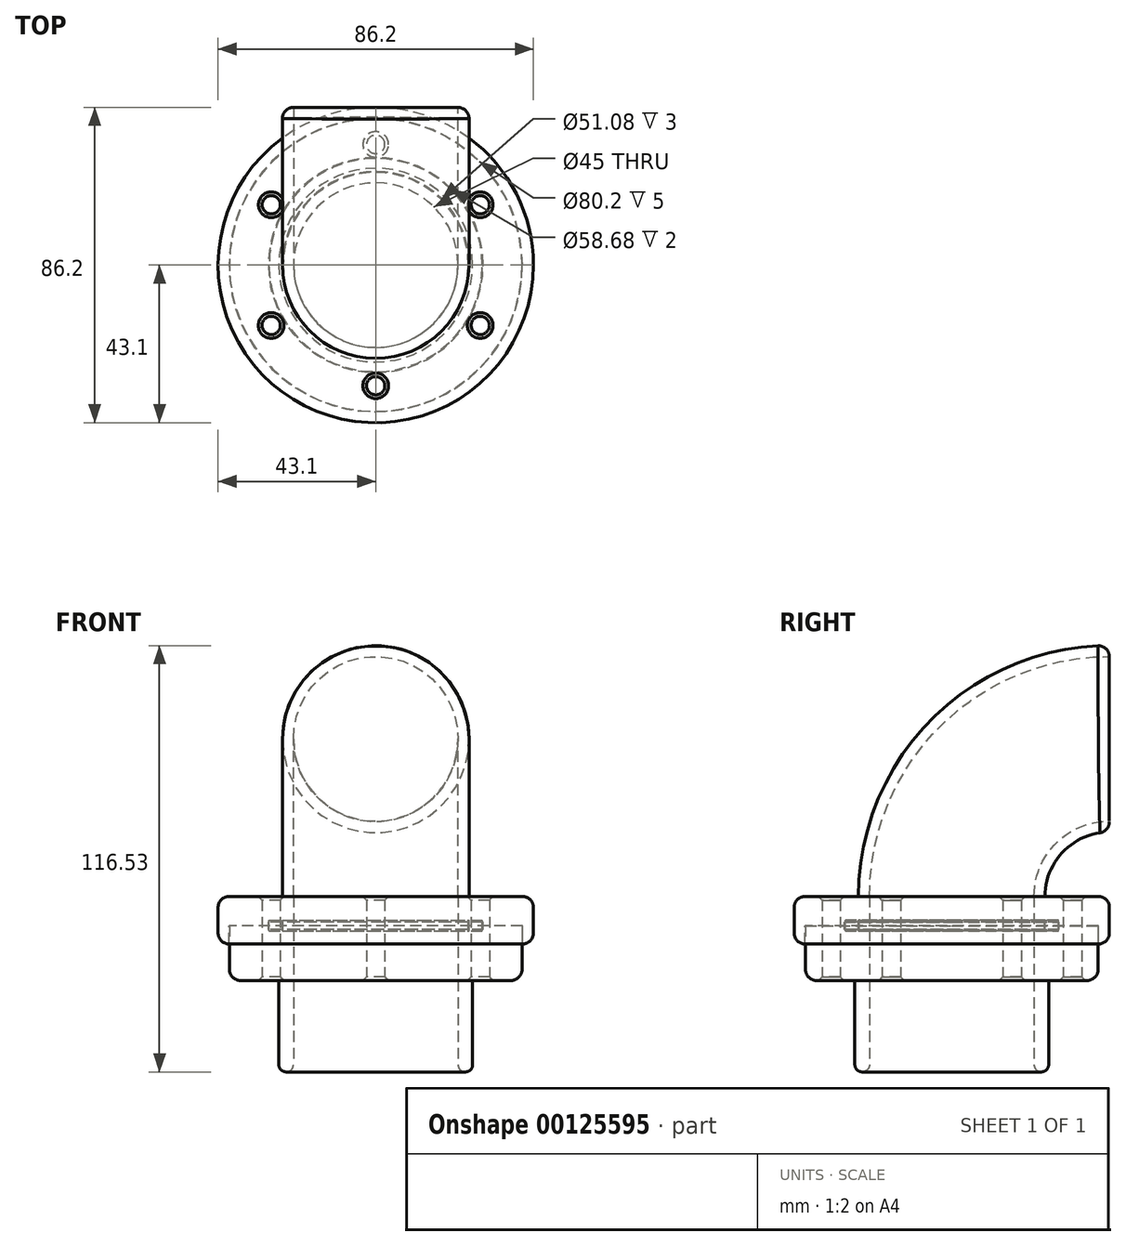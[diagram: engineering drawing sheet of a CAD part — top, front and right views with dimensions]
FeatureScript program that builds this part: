
annotation { "Feature Type Name" : "Feature", "Feature Type Description" : "" }
export const myFeature = defineFeature(function(context is Context, id is Id, definition is map)
    precondition{}
    {
        {
            var Q0;
            Q0=qCreatedBy(makeId("Top.planeOp"),FACE);
            var sketch = newSketch(context, id + "F0", { "sketchPlane" : qUnion([Q0])});
            skCircle(sketch, "E0", {"center": v(0, 0) * mm, "radius": 40 * mm});
            skCircle(sketch, "E1", {"center": v(0, 0) * mm, "radius": 22.5 * mm});
            skLineSegment(sketch, "E2", {"start": v(0, 50.57) * mm, "end": v(0, -55.17) * mm, "construction": true});
            skCircle(sketch, "E3", {"center": v(0, 33) * mm, "radius": 2.5 * mm});
            skCircle(sketch, "E4.1.0", {"center": v(-28.58, 16.5) * mm, "radius": 2.5 * mm});
            skCircle(sketch, "E4.2.0", {"center": v(-28.58, -16.5) * mm, "radius": 2.5 * mm});
            skCircle(sketch, "E4.3.0", {"center": v(0, -33) * mm, "radius": 2.5 * mm});
            skCircle(sketch, "E4.4.0", {"center": v(28.58, -16.5) * mm, "radius": 2.5 * mm});
            skCircle(sketch, "E4.5.0", {"center": v(28.58, 16.5) * mm, "radius": 2.5 * mm});
            skSolve(sketch);
        }
        {
            var Q0;
            Q0=makeQuery(id+"F0.imprint","IMPRINT",FACE,{"disambiguationData":[TD([[makeQuery(id+"F0.imprint","IMPRINT",EDGE,{"derivedFrom":sQuery(id+"F0.wireOp",EDGE,"E0")}),1.0]])]});
            extrude(context, id + "F1", {"entities" : qUnion([Q0]), "depth" : 15 * mm});
        }
        {
            var Q0;
            Q0=makeQuery(id+"F1.opExtrude","CAP_FACE",FACE,{"disambiguationData":[OSD([sQuery(id+"F0.wireOp",EDGE,"E0"),sQuery(id+"F0.wireOp",EDGE,"E1"),sQuery(id+"F0.wireOp",EDGE,"E3"),sQuery(id+"F0.wireOp",EDGE,"E4.1.0"),sQuery(id+"F0.wireOp",EDGE,"E4.2.0"),sQuery(id+"F0.wireOp",EDGE,"E4.3.0"),sQuery(id+"F0.wireOp",EDGE,"E4.4.0"),sQuery(id+"F0.wireOp",EDGE,"E4.5.0")])],"isStart":false});
            var sketch = newSketch(context, id + "F2", { "sketchPlane" : qUnion([Q0])});
            skCircle(sketch, "E5", {"center": v(0, 0) * mm, "radius": 29.34 * mm});
            skCircle(sketch, "E6", {"center": v(0, 0) * mm, "radius": 25.34 * mm});
            skSolve(sketch);
        }
        {
            var Q0;
            Q0=makeQuery(id+"F2.imprint","IMPRINT",FACE,{"disambiguationData":[TD([[makeQuery(id+"F2.imprint","IMPRINT",EDGE,{"derivedFrom":sQuery(id+"F2.wireOp",EDGE,"E5")}),1.0]])]});
            extrude(context, id + "F3", {"entities" : qUnion([Q0]), "operationType" : NewBodyOperationType.REMOVE, "oppositeDirection" : true, "depth" : 1 * mm});
        }
        {
            var Q0;
            Q0=makeQuery(id+"F1.opExtrude","CAP_FACE",FACE,{"disambiguationData":[OSD([sQuery(id+"F0.wireOp",EDGE,"E0"),sQuery(id+"F0.wireOp",EDGE,"E1"),sQuery(id+"F0.wireOp",EDGE,"E3"),sQuery(id+"F0.wireOp",EDGE,"E4.1.0"),sQuery(id+"F0.wireOp",EDGE,"E4.2.0"),sQuery(id+"F0.wireOp",EDGE,"E4.3.0"),sQuery(id+"F0.wireOp",EDGE,"E4.4.0"),sQuery(id+"F0.wireOp",EDGE,"E4.5.0")])],"isStart":true});
            var sketch = newSketch(context, id + "F4", { "sketchPlane" : qUnion([Q0])});
            skCircle(sketch, "E7", {"center": v(0, 0) * mm, "radius": 26.5 * mm});
            skSolve(sketch);
        }
        {
            var Q0;
            Q0=makeQuery(id+"F4.imprint","IMPRINT",FACE,{"disambiguationData":[TD([[makeQuery(id+"F4.imprint","IMPRINT",EDGE,{"derivedFrom":sQuery(id+"F4.wireOp",EDGE,"E7")}),1.0]])]});
            extrude(context, id + "F5", {"entities" : qUnion([Q0]), "operationType" : NewBodyOperationType.ADD, "depth" : 25 * mm});
        }
        {
            var Q0;
            Q0=makeQuery(id+"F5.opExtrude","CAP_EDGE",EDGE,{"disambiguationData":[OSD([sQuery(id+"F4.wireOp",EDGE,"E7")])],"isStart":true});
            var Q1;
            Q1=makeQuery(id+"F1.opExtrude","CAP_EDGE",EDGE,{"disambiguationData":[OSD([sQuery(id+"F0.wireOp",EDGE,"E0")])],"isStart":true});
            fillet(context, id + "F6", {"entities" : qUnion([Q0, Q1]), "radius" : 3 * mm, "tangentPropagation" : true, "allowEdgeOverflow" : false});
        }
        {
            var Q0;
            Q0=makeQuery(id+"F5.opExtrude","CAP_EDGE",EDGE,{"disambiguationData":[OSD([sQuery(id+"F4.wireOp",EDGE,"E7")])],"isStart":false});
            var Q1;
            Q1=makeQuery(id+"F5.opExtrude","CAP_EDGE",EDGE,{"disambiguationData":[OSD([sQuery(id+"F0.wireOp",EDGE,"E1")])],"isStart":false});
            fillet(context, id + "F7", {"entities" : qUnion([Q0, Q1]), "radius" : 2 * mm, "tangentPropagation" : true, "allowEdgeOverflow" : false});
        }
        {
            var Q0;
            Q0=makeQuery(id+"F1.opExtrude","CAP_EDGE",EDGE,{"disambiguationData":[OSD([sQuery(id+"F0.wireOp",EDGE,"E4.5.0")])],"isStart":true});
            var Q1;
            Q1=makeQuery(id+"F1.opExtrude","CAP_EDGE",EDGE,{"disambiguationData":[OSD([sQuery(id+"F0.wireOp",EDGE,"E4.4.0")])],"isStart":true});
            var Q2;
            Q2=makeQuery(id+"F1.opExtrude","CAP_EDGE",EDGE,{"disambiguationData":[OSD([sQuery(id+"F0.wireOp",EDGE,"E4.3.0")])],"isStart":true});
            var Q3;
            Q3=makeQuery(id+"F1.opExtrude","CAP_EDGE",EDGE,{"disambiguationData":[OSD([sQuery(id+"F0.wireOp",EDGE,"E4.1.0")])],"isStart":true});
            var Q4;
            Q4=makeQuery(id+"F1.opExtrude","CAP_EDGE",EDGE,{"disambiguationData":[OSD([sQuery(id+"F0.wireOp",EDGE,"E4.2.0")])],"isStart":true});
            var Q5;
            Q5=makeQuery(id+"F1.opExtrude","CAP_EDGE",EDGE,{"disambiguationData":[OSD([sQuery(id+"F0.wireOp",EDGE,"E3")])],"isStart":true});
            chamfer(context, id + "F8", {"entities" : qUnion([Q0, Q1, Q2, Q3, Q4, Q5]), "width" : 1 * mm, "tangentPropagation" : true});
        }
        {
            var Q0;
            {var subQ0=sQuery(id+"F0.wireOp",EDGE,"E4.2.0");var subQ1=sQuery(id+"F0.wireOp",EDGE,"E4.1.0");var subQ2=sQuery(id+"F0.wireOp",EDGE,"E3");var subQ3=sQuery(id+"F0.wireOp",EDGE,"E0");var subQ4=sQuery(id+"F0.wireOp",EDGE,"E4.3.0");var subQ5=sQuery(id+"F0.wireOp",EDGE,"E4.4.0");var subQ6=sQuery(id+"F0.wireOp",EDGE,"E4.5.0");Q0=makeQuery(id+"F3.boolean.opBoolean","SPLIT",FACE,{"disambiguationData":[TD([makeQuery(id+"F1.opExtrude","SWEPT_FACE",FACE,{"disambiguationData":[OSD([subQ3])]})])],"derivedFrom":makeQuery(id+"F1.opExtrude","CAP_FACE",FACE,{"disambiguationData":[OSD([subQ3,sQuery(id+"F0.wireOp",EDGE,"E1"),subQ2,subQ1,subQ0,subQ4,subQ5,subQ6])],"isStart":false})});}
            var sketch = newSketch(context, id + "F9", { "sketchPlane" : qUnion([Q0])});
            skCircle(sketch, "E8", {"center": v(0, 0) * mm, "radius": 40.1 * mm});
            skCircle(sketch, "E9", {"center": v(0, 0) * mm, "radius": 43.1 * mm});
            skCircle(sketch, "E10.0", {"center": v(0, 0) * mm, "radius": 22.5 * mm});
            skCircle(sketch, "E11.0", {"center": v(0, 0) * mm, "radius": 25.34 * mm});
            skCircle(sketch, "E12.0", {"center": v(0, 0) * mm, "radius": 29.34 * mm});
            skSolve(sketch);
        }
        {
            var Q0;
            Q0=makeQuery(id+"F9.imprint","IMPRINT",FACE,{"disambiguationData":[TD([[makeQuery(id+"F9.imprint","IMPRINT",EDGE,{"derivedFrom":sQuery(id+"F9.wireOp",EDGE,"E8")}),-1.0]])]});
            extrude(context, id + "F10", {"entities" : qUnion([Q0]), "oppositeDirection" : true, "depth" : 5 * mm});
        }
        {
            var Q0;
            Q0 = qSketchRegion(id + "F9", true);
            var Q1;
            Q1=makeQuery(id+"F9.imprint","IMPRINT",FACE,{"disambiguationData":[TD([[makeQuery(id+"F9.imprint","IMPRINT",EDGE,{"derivedFrom":sQuery(id+"F9.wireOp",EDGE,"E12.0")}),-1.0]])]});
            var Q2;
            Q2=makeQuery(id+"F9.imprint","IMPRINT",FACE,{"disambiguationData":[TD([[makeQuery(id+"F9.imprint","IMPRINT",EDGE,{"derivedFrom":sQuery(id+"F9.wireOp",EDGE,"E11.0")}),-1.0]])]});
            var Q3;
            Q3=makeQuery(id+"F9.imprint","IMPRINT",FACE,{"disambiguationData":[TD([[makeQuery(id+"F9.imprint","IMPRINT",EDGE,{"derivedFrom":sQuery(id+"F9.wireOp",EDGE,"E10.0")}),-1.0]])]});
            var Q4;
            Q4=makeQuery(id+"F9.imprint","IMPRINT",FACE,{"disambiguationData":[TD([[makeQuery(id+"F9.imprint","IMPRINT",EDGE,{"derivedFrom":sQuery(id+"F9.wireOp",EDGE,"E8")}),1.0]])]});
            extrude(context, id + "F11", {"entities" : qUnion([Q0, Q1, Q2, Q3, Q4]), "operationType" : NewBodyOperationType.ADD, "depth" : 8 * mm});
        }
        {
            var Q0;
            Q0=makeQuery(id+"F9.imprint","IMPRINT",FACE,{"disambiguationData":[TD([[makeQuery(id+"F9.imprint","IMPRINT",EDGE,{"derivedFrom":sQuery(id+"F9.wireOp",EDGE,"E11.0")}),-1.0]])]});
            extrude(context, id + "F12", {"entities" : qUnion([Q0]), "operationType" : NewBodyOperationType.REMOVE, "depth" : 1 * mm});
        }
        {
            var Q0;
            Q0=qCreatedBy(makeId("Right.planeOp"),FACE);
            var sketch = newSketch(context, id + "F13", { "sketchPlane" : qUnion([Q0])});
            skLineSegment(sketch, "E13.0", {"start": v(-43.1, 23) * mm, "end": v(43.1, 23) * mm});
            skArc(sketch, "E14", {"start": v(0, 23) * mm, "mid": v(12.62, 53.48) * mm, "end": v(43.1, 66.1) * mm});
            skSolve(sketch);
        }
        {
            var Q0;
            Q0=makeQuery(id+"F11.opExtrude","CAP_FACE",FACE,{"disambiguationData":[OSD([sQuery(id+"F0.wireOp",EDGE,"E3"),sQuery(id+"F0.wireOp",EDGE,"E4.1.0"),sQuery(id+"F0.wireOp",EDGE,"E4.2.0"),sQuery(id+"F0.wireOp",EDGE,"E4.3.0"),sQuery(id+"F0.wireOp",EDGE,"E4.4.0"),sQuery(id+"F0.wireOp",EDGE,"E4.5.0"),sQuery(id+"F9.wireOp",EDGE,"E9"),sQuery(id+"F9.wireOp",EDGE,"E10.0")])],"isStart":false});
            var sketch = newSketch(context, id + "F14", { "sketchPlane" : qUnion([Q0])});
            skCircle(sketch, "E15.0", {"center": v(0, 0) * mm, "radius": 22.5 * mm});
            skCircle(sketch, "E16", {"center": v(0, 0) * mm, "radius": 25.5 * mm});
            skSolve(sketch);
        }
        {
            var Q0;
            Q0=makeQuery(id+"F14.imprint","IMPRINT",FACE,{"disambiguationData":[TD([[makeQuery(id+"F14.imprint","IMPRINT",EDGE,{"derivedFrom":sQuery(id+"F14.wireOp",EDGE,"E15.0")}),-1.0]])]});
            var Q1;
            Q1=sQuery(id+"F13.wireOp",EDGE,"E14");
            sweep(context, id + "F15", {"operationType" : NewBodyOperationType.ADD, "profiles" : qUnion([Q0]), "path" : qUnion([Q1])});
        }
        {
            var Q0;
            Q0=makeQuery(id+"F15.opSweep","CAP_EDGE",EDGE,{"disambiguationData":[OSD([sQuery(id+"F13.wireOp",VERTEX,"E14.start"),sQuery(id+"F14.wireOp",EDGE,"E16")])],"isStart":true});
            var Q1;
            Q1=makeQuery(id+"F11.opExtrude","CAP_EDGE",EDGE,{"disambiguationData":[OSD([sQuery(id+"F9.wireOp",EDGE,"E9")])],"isStart":false});
            var Q2;
            Q2=makeQuery(id+"F15.opSweep","CAP_EDGE",EDGE,{"disambiguationData":[OSD([sQuery(id+"F13.wireOp",VERTEX,"E14.end"),sQuery(id+"F14.wireOp",EDGE,"E16")])],"isStart":false});
            var Q3;
            Q3=makeQuery(id+"F10.opExtrude","CAP_EDGE",EDGE,{"disambiguationData":[OSD([sQuery(id+"F9.wireOp",EDGE,"E9")])],"isStart":false});
            fillet(context, id + "F16", {"entities" : qUnion([Q0, Q1, Q2, Q3]), "radius" : 3 * mm, "tangentPropagation" : true, "allowEdgeOverflow" : false});
        }
        {
            var Q0;
            Q0=makeQuery(id+"F11.opExtrude","CAP_EDGE",EDGE,{"disambiguationData":[OSD([sQuery(id+"F0.wireOp",EDGE,"E4.3.0")])],"isStart":false});
            var Q1;
            Q1=makeQuery(id+"F11.opExtrude","CAP_EDGE",EDGE,{"disambiguationData":[OSD([sQuery(id+"F0.wireOp",EDGE,"E4.4.0")])],"isStart":false});
            var Q2;
            Q2=makeQuery(id+"F11.opExtrude","CAP_EDGE",EDGE,{"disambiguationData":[OSD([sQuery(id+"F0.wireOp",EDGE,"E4.2.0")])],"isStart":false});
            var Q3;
            Q3=makeQuery(id+"F11.opExtrude","CAP_EDGE",EDGE,{"disambiguationData":[OSD([sQuery(id+"F0.wireOp",EDGE,"E4.1.0")])],"isStart":false});
            var Q4;
            Q4=makeQuery(id+"F11.opExtrude","CAP_EDGE",EDGE,{"disambiguationData":[OSD([sQuery(id+"F0.wireOp",EDGE,"E3")])],"isStart":false});
            var Q5;
            Q5=makeQuery(id+"F11.opExtrude","CAP_EDGE",EDGE,{"disambiguationData":[OSD([sQuery(id+"F0.wireOp",EDGE,"E4.5.0")])],"isStart":false});
            chamfer(context, id + "F17", {"entities" : qUnion([Q0, Q1, Q2, Q3, Q4, Q5]), "width" : 1 * mm, "tangentPropagation" : true});
        }
        {
            var Q0;
            {var subQ0=sQuery(id+"F9.wireOp",EDGE,"E10.0");Q0=makeQuery(id+"F12.boolean.opBoolean","SPLIT",FACE,{"disambiguationData":[TD([makeQuery(id+"F11.opExtrude","SWEPT_FACE",FACE,{"disambiguationData":[OSD([subQ0])]})])],"derivedFrom":makeQuery(id+"F11.opExtrude","CAP_FACE",FACE,{"disambiguationData":[OSD([sQuery(id+"F0.wireOp",EDGE,"E3"),sQuery(id+"F0.wireOp",EDGE,"E4.1.0"),sQuery(id+"F0.wireOp",EDGE,"E4.2.0"),sQuery(id+"F0.wireOp",EDGE,"E4.3.0"),sQuery(id+"F0.wireOp",EDGE,"E4.4.0"),sQuery(id+"F0.wireOp",EDGE,"E4.5.0"),sQuery(id+"F9.wireOp",EDGE,"E9"),subQ0])],"isStart":true})});}
            var sketch = newSketch(context, id + "F18", { "sketchPlane" : qUnion([Q0])});
            skCircle(sketch, "E17.0.0", {"center": v(0, 0) * mm, "radius": 29.34 * mm});
            skCircle(sketch, "E18.0", {"center": v(0, 0) * mm, "radius": 25.34 * mm});
            skCircle(sketch, "E19", {"center": v(0, 0) * mm, "radius": 29.14 * mm});
            skCircle(sketch, "E20", {"center": v(0, 0) * mm, "radius": 25.54 * mm});
            skSolve(sketch);
        }
        {
            var Q0;
            Q0=makeQuery(id+"F18.imprint","IMPRINT",FACE,{"disambiguationData":[TD([[makeQuery(id+"F18.imprint","IMPRINT",EDGE,{"derivedFrom":sQuery(id+"F18.wireOp",EDGE,"E19")}),1.0]])]});
            extrude(context, id + "F19", {"entities" : qUnion([Q0]), "endBound" : BoundingType.SYMMETRIC, "depth" : 3 * mm});
        }
    });
